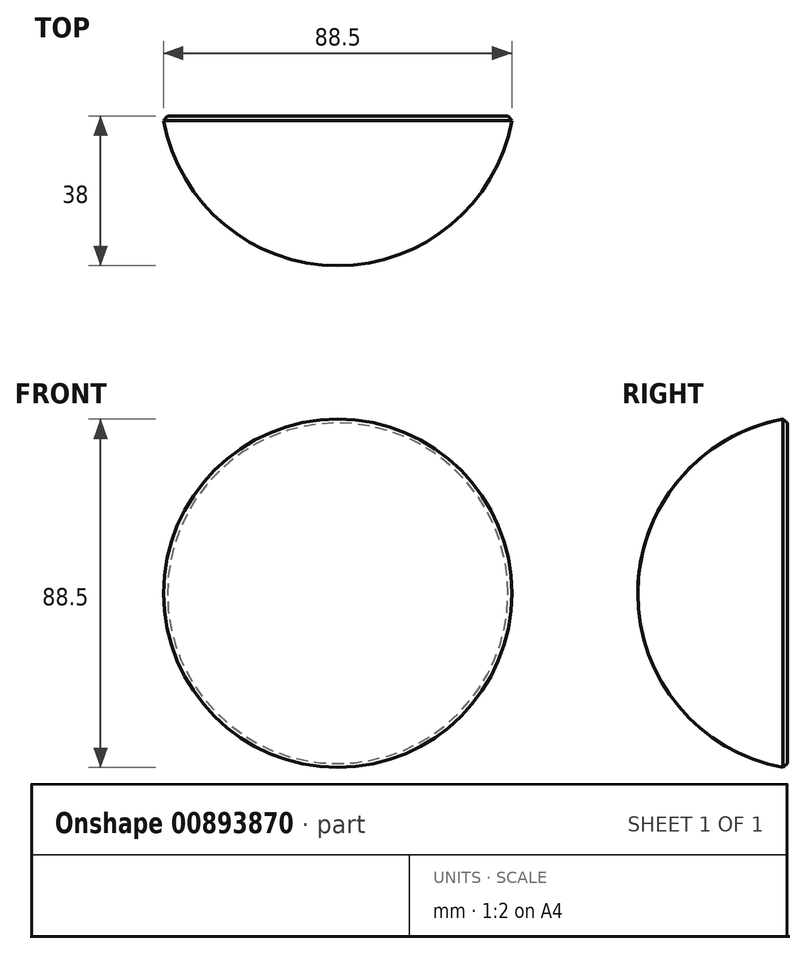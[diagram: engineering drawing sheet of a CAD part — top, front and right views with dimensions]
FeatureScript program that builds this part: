
annotation { "Feature Type Name" : "Feature", "Feature Type Description" : "" }
export const myFeature = defineFeature(function(context is Context, id is Id, definition is map)
    precondition{}
    {
        {
            var Q0;
            Q0=qCreatedBy(makeId("Right.planeOp"),FACE);
            var sketch = newSketch(context, id + "F0", { "sketchPlane" : qUnion([Q0])});
            skArc(sketch, "E0", {"start": v(-7, 44.45) * mm, "mid": v(-34.2, 29.24) * mm, "end": v(-45, 0) * mm});
            skLineSegment(sketch, "E1", {"start": v(-7, 44.45) * mm, "end": v(-7, 0) * mm});
            skLineSegment(sketch, "E2", {"start": v(-45, 0) * mm, "end": v(-7, 0) * mm});
            skPoint(sketch, "E3.orphan", {"position": v(-7, -44.45) * mm});
            skSolve(sketch);
        }
        {
            var Q0;
            Q0=makeQuery(id+"F0.imprint","IMPRINT",FACE,{"disambiguationData":[TD([[makeQuery(id+"F0.imprint","IMPRINT",EDGE,{"derivedFrom":sQuery(id+"F0.wireOp",EDGE,"E0")}),1.0]])]});
            var Q1;
            Q1=sQuery(id+"F0.wireOp",EDGE,"E2");
            revolve(context, id + "F1", {"surfaceOperationType" : NewSurfaceOperationType.NEW, "entities" : qUnion([Q0]), "axis" : qUnion([Q1]), "revolveType" : RevolveType.FULL});
        }
        {
            var Q0;
            Q0=makeQuery(id+"F1.opRevolve","SWEPT_EDGE",EDGE,{"disambiguationData":[OSD([sQuery(id+"F0.wireOp",EDGE,"E0"),sQuery(id+"F0.wireOp",EDGE,"E1")])]});
            chamfer(context, id + "F2", {"entities" : qUnion([Q0]), "width" : 1 * mm, "tangentPropagation" : true});
        }
        {
            var Q0;
            Q0=qCreatedBy(makeId("Right.planeOp"),FACE);
            var sketch = newSketch(context, id + "F3", { "sketchPlane" : qUnion([Q0])});
            skLineSegment(sketch, "E4.bottom", {"start": v(51.47, 36.02) * mm, "end": v(37.15, 36.02) * mm});
            skLineSegment(sketch, "E4.top", {"start": v(51.47, 52.82) * mm, "end": v(37.15, 52.82) * mm});
            skLineSegment(sketch, "E4.left", {"start": v(51.47, 36.02) * mm, "end": v(51.47, 52.82) * mm});
            skLineSegment(sketch, "E4.right", {"start": v(37.15, 36.02) * mm, "end": v(37.15, 52.82) * mm});
            skSolve(sketch);
        }
        {
            var Q0;
            Q0=makeQuery(id+"F3.imprint","IMPRINT",FACE,{"disambiguationData":[TD([[makeQuery(id+"F3.imprint","IMPRINT",EDGE,{"derivedFrom":sQuery(id+"F3.wireOp",EDGE,"E4.bottom")}),-1.0]])]});
            extrude(context, id + "F4", {"entities" : qUnion([Q0]), "depth" : 25 * mm, "offsetDistance" : 25 * mm});
        }
        {
            var Q0;
            Q0=makeQuery(id+"F4.opExtrude","SWEPT_BODY",BODY,{"disambiguationData":[OSD([sQuery(id+"F3.wireOp",EDGE,"E4.bottom"),sQuery(id+"F3.wireOp",EDGE,"E4.top"),sQuery(id+"F3.wireOp",EDGE,"E4.left"),sQuery(id+"F3.wireOp",EDGE,"E4.right")])]});
            deleteBodies(context, id + "F5", {"entities" : qUnion([Q0])});
        }
    });
